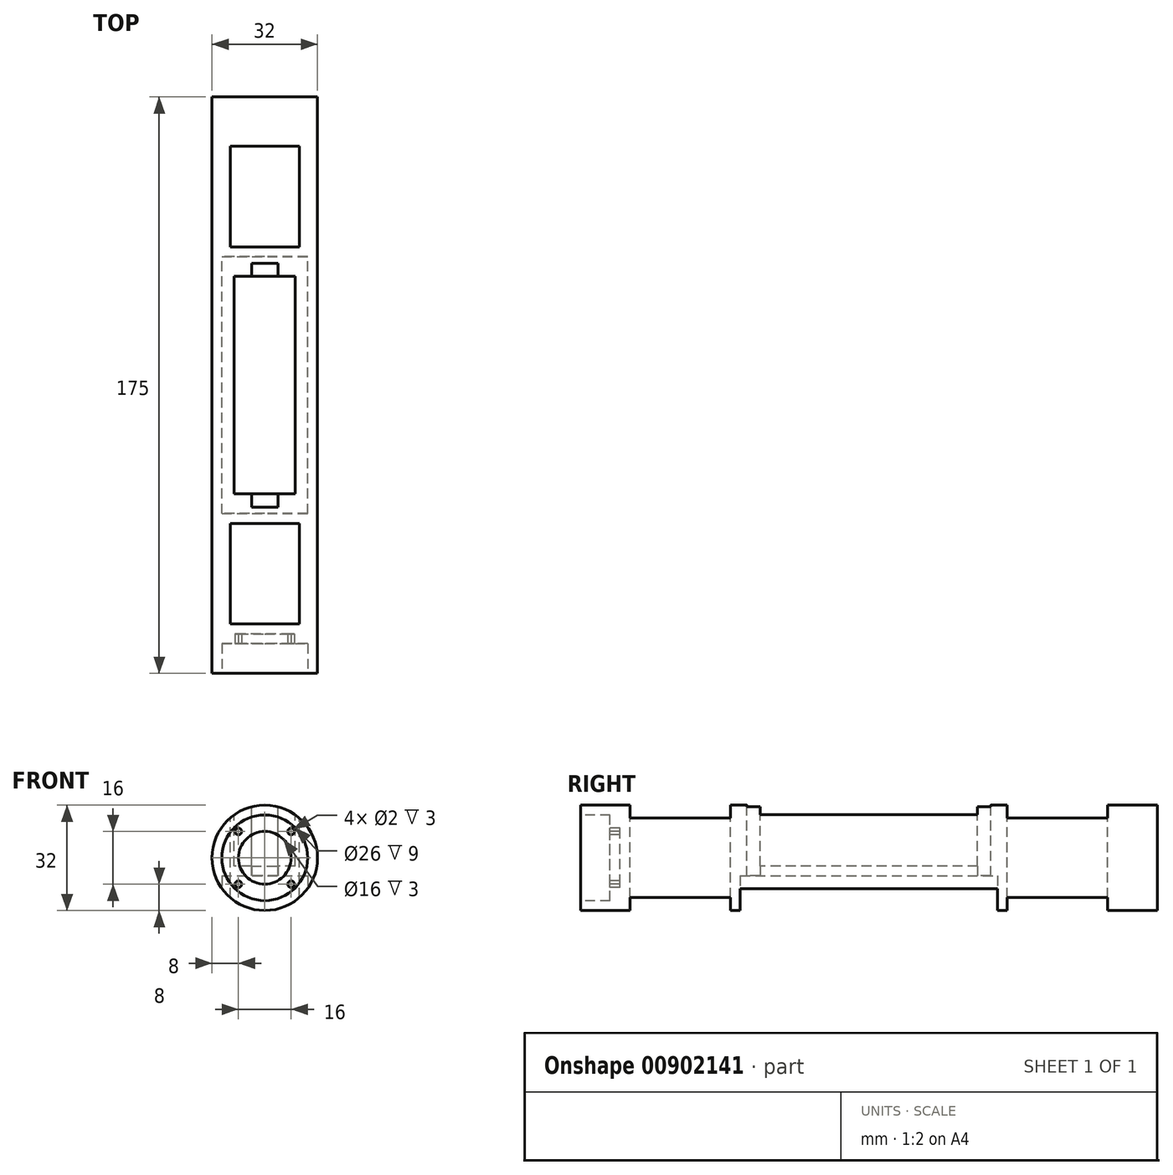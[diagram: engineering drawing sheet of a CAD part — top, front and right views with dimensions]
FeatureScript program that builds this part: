
annotation { "Feature Type Name" : "Feature", "Feature Type Description" : "" }
export const myFeature = defineFeature(function(context is Context, id is Id, definition is map)
    precondition{}
    {
        {
            assignVariable(context, id + "F0", {"name" : "width", "anyValue" : 32 * mm});
        }
        {
            assignVariable(context, id + "F1", {"name" : "thickness", "anyValue" : 3 * mm});
        }
        {
            assignVariable(context, id + "F2", {"name" : "motor_w", "anyValue" : 21 * mm});
        }
        {
            assignVariable(context, id + "F3", {"name" : "inset_l", "anyValue" : 12 * mm});
        }
        {
            assignVariable(context, id + "F4", {"name" : "battery_r", "anyValue" : 18.5 * mm});
        }
        {
            var Q0;
            Q0=qCreatedBy(makeId("Top.planeOp"),FACE);
            var sketch = newSketch(context, id + "F5", { "sketchPlane" : qUnion([Q0])});
            skLineSegment(sketch, "E0.bottom", {"start": v(-16, 87.5) * mm, "end": v(16, 87.5) * mm});
            skLineSegment(sketch, "E0.top", {"start": v(-16, -87.5) * mm, "end": v(16, -87.5) * mm});
            skLineSegment(sketch, "E0.left", {"start": v(-16, 87.5) * mm, "end": v(-16, -87.5) * mm});
            skLineSegment(sketch, "E0.right", {"start": v(16, 87.5) * mm, "end": v(16, -87.5) * mm});
            skPoint(sketch, "E0.middle", {"position": v(0, 0) * mm});
            skSolve(sketch);
        }
        {
            var Q0;
            Q0=makeQuery(id+"F5.imprint","IMPRINT",FACE,{"disambiguationData":[TD([[makeQuery(id+"F5.imprint","IMPRINT",EDGE,{"derivedFrom":sQuery(id+"F5.wireOp",EDGE,"E0.bottom")}),-1.0]])]});
            extrude(context, id + "F6", {"entities" : qUnion([Q0]), "depth" : getVariable(context, 'width'), "offsetDistance" : 25 * mm, "symmetric" : true});
        }
        {
            var Q0;
            Q0=makeQuery(id+"F6.opExtrude","CAP_FACE",FACE,{"disambiguationData":[OSD([sQuery(id+"F5.wireOp",EDGE,"E0.bottom"),sQuery(id+"F5.wireOp",EDGE,"E0.top"),sQuery(id+"F5.wireOp",EDGE,"E0.left"),sQuery(id+"F5.wireOp",EDGE,"E0.right")])],"isStart":false});
            var sketch = newSketch(context, id + "F7", { "sketchPlane" : qUnion([Q0])});
            skLineSegment(sketch, "E1.bottom", {"start": v(-10.5, 72.5) * mm, "end": v(10.5, 72.5) * mm});
            skLineSegment(sketch, "E1.top", {"start": v(-10.5, 42) * mm, "end": v(10.5, 42) * mm});
            skLineSegment(sketch, "E1.left", {"start": v(-10.5, 72.5) * mm, "end": v(-10.5, 42) * mm});
            skLineSegment(sketch, "E1.right", {"start": v(10.5, 72.5) * mm, "end": v(10.5, 42) * mm});
            skPoint(sketch, "E1.middle", {"position": v(0, 57.25) * mm});
            skLineSegment(sketch, "E2.bottom", {"start": v(-10.5, -42) * mm, "end": v(10.5, -42) * mm});
            skLineSegment(sketch, "E2.top", {"start": v(-10.5, -72.5) * mm, "end": v(10.5, -72.5) * mm});
            skLineSegment(sketch, "E2.left", {"start": v(-10.5, -42) * mm, "end": v(-10.5, -72.5) * mm});
            skLineSegment(sketch, "E2.right", {"start": v(10.5, -42) * mm, "end": v(10.5, -72.5) * mm});
            skPoint(sketch, "E2.middle", {"position": v(0, -57.25) * mm});
            skSolve(sketch);
        }
        {
            var Q0;
            Q0=makeQuery(id+"F7.imprint","IMPRINT",FACE,{"disambiguationData":[TD([[makeQuery(id+"F7.imprint","IMPRINT",EDGE,{"derivedFrom":sQuery(id+"F7.wireOp",EDGE,"E1.bottom")}),-1.0]])]});
            var Q1;
            Q1=makeQuery(id+"F7.imprint","IMPRINT",FACE,{"disambiguationData":[TD([[makeQuery(id+"F7.imprint","IMPRINT",EDGE,{"derivedFrom":sQuery(id+"F7.wireOp",EDGE,"E2.bottom")}),-1.0]])]});
            extrude(context, id + "F8", {"entities" : qUnion([Q0, Q1]), "operationType" : NewBodyOperationType.REMOVE, "endBound" : BoundingType.THROUGH_ALL, "oppositeDirection" : true, "depth" : (getVariable(context, 'width') / 2) + (getVariable(context, 'motor_w') / 2), "offsetDistance" : 25 * mm});
        }
        {
            var Q0;
            Q0=makeQuery(id+"F6.opExtrude","CAP_FACE",FACE,{"disambiguationData":[OSD([sQuery(id+"F5.wireOp",EDGE,"E0.bottom"),sQuery(id+"F5.wireOp",EDGE,"E0.top"),sQuery(id+"F5.wireOp",EDGE,"E0.left"),sQuery(id+"F5.wireOp",EDGE,"E0.right")])],"isStart":false});
            var sketch = newSketch(context, id + "F9", { "sketchPlane" : qUnion([Q0])});
            skLineSegment(sketch, "E3.bottom", {"start": v(9.25, 33) * mm, "end": v(-9.25, 33) * mm});
            skLineSegment(sketch, "E3.top", {"start": v(9.25, -33) * mm, "end": v(-9.25, -33) * mm});
            skLineSegment(sketch, "E3.left", {"start": v(9.25, 33) * mm, "end": v(9.25, -33) * mm});
            skLineSegment(sketch, "E3.right", {"start": v(-9.25, 33) * mm, "end": v(-9.25, -33) * mm});
            skPoint(sketch, "E3.middle", {"position": v(0, 0) * mm});
            skLineSegment(sketch, "E4.bottom", {"start": v(4, 37) * mm, "end": v(-4, 37) * mm});
            skLineSegment(sketch, "E4.top", {"start": v(4, -37) * mm, "end": v(-4, -37) * mm});
            skLineSegment(sketch, "E4.left", {"start": v(4, 37) * mm, "end": v(4, -37) * mm});
            skLineSegment(sketch, "E4.right", {"start": v(-4, 37) * mm, "end": v(-4, -37) * mm});
            skSolve(sketch);
        }
        {
            var Q0;
            Q0=makeQuery(id+"F9.imprint","IMPRINT",FACE,{"disambiguationData":[TD([[makeQuery(id+"F9.imprint","IMPRINT",EDGE,{"derivedFrom":sQuery(id+"F9.wireOp",EDGE,"E3.bottom")}),1.0]])]});
            var Q1;
            {var subQ5=sQuery(id+"F9.wireOp",EDGE,"E4.bottom");Q1=makeQuery(id+"F9.imprint","IMPRINT",FACE,{"disambiguationData":[TD([[makeQuery(id+"F9.imprint","IMPRINT",EDGE,{"derivedFrom":subQ5}),1.0]])]});}
            var Q2;
            {var subQ5=sQuery(id+"F9.wireOp",EDGE,"E4.top");Q2=makeQuery(id+"F9.imprint","IMPRINT",FACE,{"disambiguationData":[TD([[makeQuery(id+"F9.imprint","IMPRINT",EDGE,{"derivedFrom":subQ5}),-1.0]])]});}
            extrude(context, id + "F10", {"entities" : qUnion([Q0, Q1, Q2]), "operationType" : NewBodyOperationType.REMOVE, "oppositeDirection" : true, "depth" : getVariable(context, 'battery_r'), "offsetDistance" : 25 * mm});
        }
        {
            var Q0;
            Q0=makeQuery(id+"F6.opExtrude","SWEPT_FACE",FACE,{"disambiguationData":[OSD([sQuery(id+"F5.wireOp",EDGE,"E0.top")])]});
            var sketch = newSketch(context, id + "F11", { "sketchPlane" : qUnion([Q0])});
            skCircle(sketch, "E5", {"center": v(0, 0) * mm, "radius": 16 * mm});
            skSolve(sketch);
        }
        {
            var Q0;
            Q0=makeQuery(id+"F6.opExtrude","CAP_FACE",FACE,{"disambiguationData":[OSD([sQuery(id+"F5.wireOp",EDGE,"E0.bottom"),sQuery(id+"F5.wireOp",EDGE,"E0.top"),sQuery(id+"F5.wireOp",EDGE,"E0.left"),sQuery(id+"F5.wireOp",EDGE,"E0.right")])],"isStart":true});
            var sketch = newSketch(context, id + "F12", { "sketchPlane" : qUnion([Q0])});
            skLineSegment(sketch, "E6.bottom", {"start": v(-13, 39) * mm, "end": v(13, 39) * mm});
            skLineSegment(sketch, "E6.top", {"start": v(-13, -39) * mm, "end": v(13, -39) * mm});
            skLineSegment(sketch, "E6.left", {"start": v(-13, 39) * mm, "end": v(-13, -39) * mm});
            skLineSegment(sketch, "E6.right", {"start": v(13, 39) * mm, "end": v(13, -39) * mm});
            skPoint(sketch, "E6.middle", {"position": v(0, 0) * mm});
            skSolve(sketch);
        }
        {
            var Q0;
            Q0=makeQuery(id+"F12.imprint","IMPRINT",FACE,{"disambiguationData":[TD([[makeQuery(id+"F12.imprint","IMPRINT",EDGE,{"derivedFrom":sQuery(id+"F12.wireOp",EDGE,"E6.bottom")}),-1.0]])]});
            extrude(context, id + "F13", {"entities" : qUnion([Q0]), "operationType" : NewBodyOperationType.REMOVE, "oppositeDirection" : true, "depth" : getVariable(context, 'width') - getVariable(context, 'thickness') - getVariable(context, 'battery_r'), "offsetDistance" : 25 * mm});
        }
        {
            var Q0;
            {var subQ0=sQuery(id+"F11.wireOp",EDGE,"E5");var subQ1=sQuery(id+"F5.wireOp",EDGE,"E0.top");var subQ2=makeQuery(id+"F11.imprint","INTERSECT",VERTEX,{"derivedFrom":[makeQuery(id+"F6.opExtrude","CAP_EDGE",EDGE,{"disambiguationData":[OSD([subQ1])],"isStart":false}),subQ0]});Q0=makeQuery(id+"F11.imprint","IMPRINT",FACE,{"disambiguationData":[TD([[makeQuery(id+"F11.imprint","IMPRINT",EDGE,{"disambiguationData":[TD([[subQ2,1.0]])],"derivedFrom":subQ0}),1.0]])]});}
            extrude(context, id + "F14", {"entities" : qUnion([Q0]), "operationType" : NewBodyOperationType.INTERSECT, "endBound" : BoundingType.THROUGH_ALL, "oppositeDirection" : true, "depth" : 25 * mm, "offsetDistance" : 25 * mm});
        }
        {
            var Q0;
            Q0=makeQuery(id+"F13.boolean.opBoolean","COPY",FACE,{"derivedFrom":makeQuery(id+"F13.opExtrude","CAP_FACE",FACE,{"disambiguationData":[OSD([sQuery(id+"F12.wireOp",EDGE,"E6.bottom"),sQuery(id+"F12.wireOp",EDGE,"E6.top"),sQuery(id+"F12.wireOp",EDGE,"E6.left"),sQuery(id+"F12.wireOp",EDGE,"E6.right")])],"isStart":false})});
            var sketch = newSketch(context, id + "F15", { "sketchPlane" : qUnion([Q0])});
            skLineSegment(sketch, "E7.0", {"start": v(4, 33) * mm, "end": v(4, 37) * mm});
            skLineSegment(sketch, "E7.1", {"start": v(-4, 33) * mm, "end": v(-4, 37) * mm});
            skLineSegment(sketch, "E7.2", {"start": v(4, -37) * mm, "end": v(4, -33) * mm});
            skLineSegment(sketch, "E7.3", {"start": v(-4, -37) * mm, "end": v(-4, -33) * mm});
            skLineSegment(sketch, "E8", {"start": v(4, 33) * mm, "end": v(-4, 33) * mm});
            skLineSegment(sketch, "E9", {"start": v(4, 37) * mm, "end": v(-4, 37) * mm});
            skLineSegment(sketch, "E10", {"start": v(4, -33) * mm, "end": v(-4, -33) * mm});
            skLineSegment(sketch, "E11", {"start": v(4, -37) * mm, "end": v(-4, -37) * mm});
            skSolve(sketch);
        }
        {
            var Q0;
            Q0=makeQuery(id+"F15.imprint","IMPRINT",FACE,{"disambiguationData":[TD([[makeQuery(id+"F15.imprint","IMPRINT",EDGE,{"derivedFrom":sQuery(id+"F15.wireOp",EDGE,"E7.0")}),1.0]])]});
            var Q1;
            Q1=makeQuery(id+"F15.imprint","IMPRINT",FACE,{"disambiguationData":[TD([[makeQuery(id+"F15.imprint","IMPRINT",EDGE,{"derivedFrom":sQuery(id+"F15.wireOp",EDGE,"E7.2")}),1.0]])]});
            extrude(context, id + "F16", {"entities" : qUnion([Q0, Q1]), "operationType" : NewBodyOperationType.REMOVE, "endBound" : BoundingType.THROUGH_ALL, "oppositeDirection" : true, "depth" : 25 * mm, "offsetDistance" : 25 * mm});
        }
        {
            var Q0;
            Q0=makeQuery(id+"F6.opExtrude","SWEPT_FACE",FACE,{"disambiguationData":[OSD([sQuery(id+"F5.wireOp",EDGE,"E0.top")])]});
            var sketch = newSketch(context, id + "F17", { "sketchPlane" : qUnion([Q0])});
            skCircle(sketch, "E12", {"center": v(0, 0) * mm, "radius": 13 * mm});
            skSolve(sketch);
        }
        {
            var Q0;
            Q0=makeQuery(id+"F17.imprint","IMPRINT",FACE,{"disambiguationData":[TD([[makeQuery(id+"F17.imprint","IMPRINT",EDGE,{"derivedFrom":sQuery(id+"F17.wireOp",EDGE,"E12")}),1.0]])]});
            extrude(context, id + "F18", {"entities" : qUnion([Q0]), "operationType" : NewBodyOperationType.REMOVE, "oppositeDirection" : true, "depth" : getVariable(context, 'inset_l') - getVariable(context, 'thickness'), "offsetDistance" : 25 * mm});
        }
        {
            var Q0;
            Q0=makeQuery(id+"F18.boolean.opBoolean","COPY",FACE,{"derivedFrom":makeQuery(id+"F18.opExtrude","CAP_FACE",FACE,{"disambiguationData":[OSD([sQuery(id+"F17.wireOp",EDGE,"E12")])],"isStart":false})});
            var sketch = newSketch(context, id + "F19", { "sketchPlane" : qUnion([Q0])});
            skLineSegment(sketch, "E13.bottom", {"start": v(8, -8) * mm, "end": v(-8, -8) * mm, "construction": true});
            skLineSegment(sketch, "E13.top", {"start": v(8, 8) * mm, "end": v(-8, 8) * mm, "construction": true});
            skLineSegment(sketch, "E13.left", {"start": v(8, -8) * mm, "end": v(8, 8) * mm, "construction": true});
            skLineSegment(sketch, "E13.right", {"start": v(-8, -8) * mm, "end": v(-8, 8) * mm, "construction": true});
            skPoint(sketch, "E13.middle", {"position": v(0, 0) * mm});
            skCircle(sketch, "E14", {"center": v(8, -8) * mm, "radius": 1 * mm});
            skCircle(sketch, "E15", {"center": v(-8, -8) * mm, "radius": 1 * mm});
            skCircle(sketch, "E16", {"center": v(-8, 8) * mm, "radius": 1 * mm});
            skCircle(sketch, "E17", {"center": v(8, 8) * mm, "radius": 1 * mm});
            skCircle(sketch, "E18", {"center": v(0, 0) * mm, "radius": 8 * mm});
            skSolve(sketch);
        }
        {
            var Q0;
            Q0 = qSketchRegion(id + "F19", true);
            extrude(context, id + "F20", {"entities" : qUnion([Q0]), "operationType" : NewBodyOperationType.REMOVE, "oppositeDirection" : true, "depth" : getVariable(context, 'thickness'), "offsetDistance" : 25 * mm});
        }
    });
